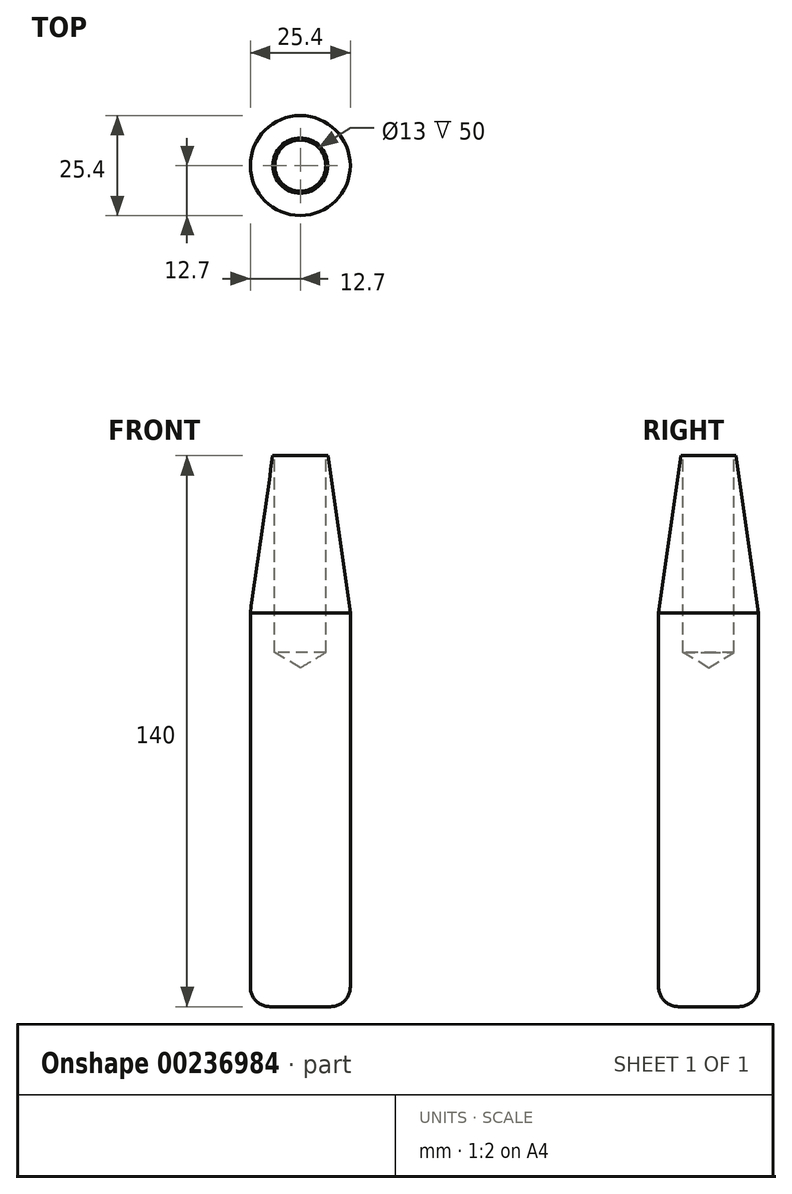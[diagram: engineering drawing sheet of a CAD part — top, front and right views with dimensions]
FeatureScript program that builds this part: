
annotation { "Feature Type Name" : "Feature", "Feature Type Description" : "" }
export const myFeature = defineFeature(function(context is Context, id is Id, definition is map)
    precondition{}
    {
        {
            var Q0;
            Q0=qCreatedBy(makeId("Front.planeOp"),FACE);
            var sketch = newSketch(context, id + "F0", { "sketchPlane" : qUnion([Q0])});
            skLineSegment(sketch, "E0", {"start": v(0, -45.79) * mm, "end": v(-12.7, -45.79) * mm});
            skLineSegment(sketch, "E1", {"start": v(-12.7, -45.79) * mm, "end": v(-12.7, 54.21) * mm});
            skLineSegment(sketch, "E2", {"start": v(0, -45.79) * mm, "end": v(0, 94.21) * mm});
            skLineSegment(sketch, "E3", {"start": v(0, 94.21) * mm, "end": v(-7, 94.21) * mm});
            skLineSegment(sketch, "E4", {"start": v(-12.7, 54.21) * mm, "end": v(-7, 94.21) * mm});
            skSolve(sketch);
        }
        {
            var Q0;
            Q0=makeQuery(id+"F0.imprint","IMPRINT",FACE,{"disambiguationData":[TD([[makeQuery(id+"F0.imprint","IMPRINT",EDGE,{"derivedFrom":sQuery(id+"F0.wireOp",EDGE,"E0")}),-1.0]])]});
            var Q1;
            Q1=sQuery(id+"F0.wireOp",EDGE,"E2");
            revolve(context, id + "F1", {"entities" : qUnion([Q0]), "axis" : qUnion([Q1]), "revolveType" : RevolveType.FULL});
        }
        {
            var Q0;
            Q0=makeQuery(id+"F1.opRevolve","SWEPT_FACE",FACE,{"disambiguationData":[OSD([sQuery(id+"F0.wireOp",EDGE,"E3")])]});
            var sketch = newSketch(context, id + "F2", { "sketchPlane" : qUnion([Q0])});
            skPoint(sketch, "E5", {"position": v(0, 0) * mm});
            skSolve(sketch);
        }
        {
            var Q0;
            Q0=sQuery(id+"F2.wireOp",VERTEX,"E5");
            var Q1;
            Q1=makeQuery(id+"F1.opRevolve","SWEPT_BODY",BODY,{"disambiguationData":[OSD([sQuery(id+"F0.wireOp",EDGE,"E0"),sQuery(id+"F0.wireOp",EDGE,"E1"),sQuery(id+"F0.wireOp",EDGE,"E2"),sQuery(id+"F0.wireOp",EDGE,"E3"),sQuery(id+"F0.wireOp",EDGE,"E4")])]});
            hole(context, id + "F3", {"style" : HoleStyle.SIMPLE, "endStyle" : HoleEndStyle.BLIND, "holeDiameter" : 13 * mm, "holeDepth" : 50 * mm, "locations" : qUnion([Q0]), "scope" : qUnion([Q1])});
        }
        {
            var Q0;
            Q0=makeQuery(id+"F1.opRevolve","SWEPT_EDGE",EDGE,{"disambiguationData":[OSD([sQuery(id+"F0.wireOp",EDGE,"E0"),sQuery(id+"F0.wireOp",EDGE,"E1")])]});
            fillet(context, id + "F4", {"entities" : qUnion([Q0]), "radius" : 5 * mm, "tangentPropagation" : true, "allowEdgeOverflow" : false});
        }
    });
